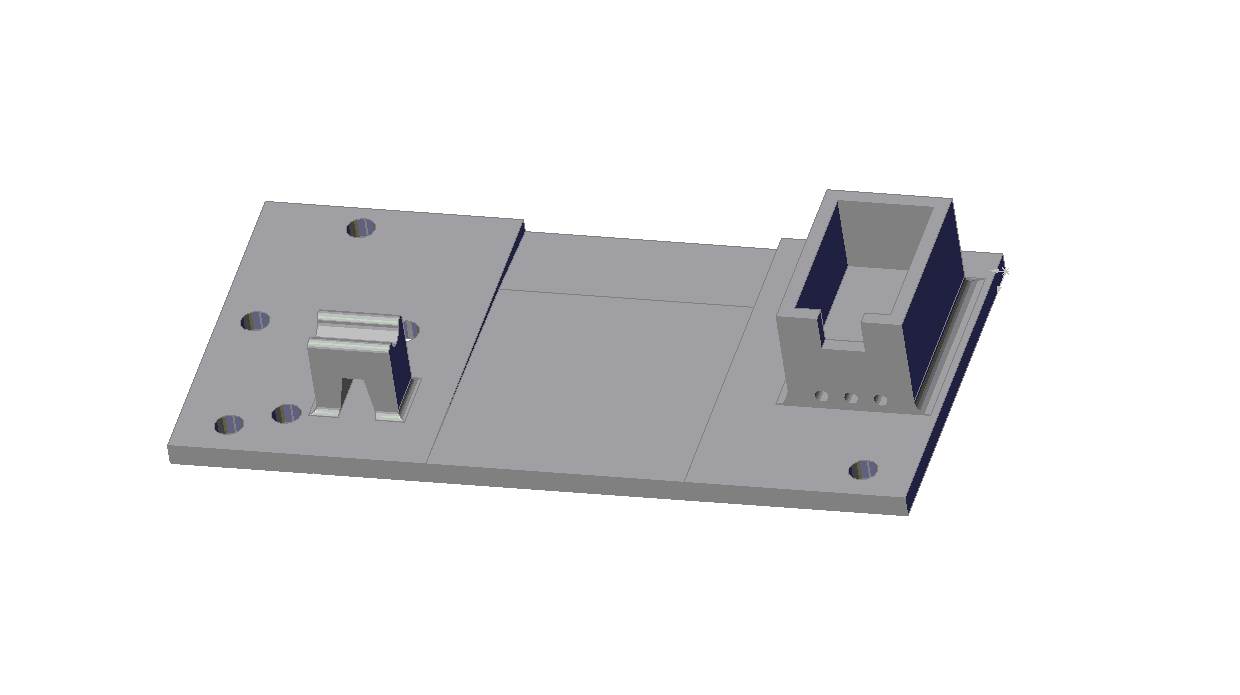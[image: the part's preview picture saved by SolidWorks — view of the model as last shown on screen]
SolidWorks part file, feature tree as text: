
SOLIDWORKS PART (.sldprt)
format: sldprt  version: not decoded by parser v0  size: 579,072 bytes
history: native  units: mm
features: sketch x13, cut_extrude x8, fillet x8, extrude x5, plane x3, material x1 (+10 scaffold rows collapsed)
feature tree (48):
  scaffold x10  (default folders/planes/origin — collapsed)
  material  "Matériau <non spécifié>"
  plane  "Plan de face"
  plane  "Plan de dessus"
  plane  "Plan de droite"
  sketch  "Esquisse1"  dims[D1=100.0mm D2=50.0mm]
  extrude  "Extrusion1"  Depth=1mm
  sketch  "Esquisse2"  dims[D1=30.0mm D2=35.0mm D3=35.0mm]
  extrude  "Extrusion2"  Depth=2mm
  sketch  "Esquisse4"  dims[D1=17.0mm D2=26.0mm]
  extrude  "Extrusion3"  Depth=15mm
  sketch  "Esquisse5"  dims[D1=2.0mm D2=2.0mm]
  cut_extrude  "Enlèv. mat.-Extru.1"  Depth=11mm
  sketch  "Esquisse6"  dims[D1=15.0mm D2=3.5mm]
  cut_extrude  "Enlèv. mat.-Extru.2"  Depth=4mm
  sketch  "Esquisse7"  dims[D1=6.0mm D2=3.5mm]
  cut_extrude  "Enlèv. mat.-Extru.3"  Depth=5mm
  sketch  "Esquisse8"  dims[D1=6.5mm D2=4.0mm D3=4.0mm]
  cut_extrude  "Enlèv. mat.-Extru.4"  Depth=8mm
  sketch  "Esquisse10"  dims[D1=7.0mm D2=5.0mm D3=5.0mm D4=7.0mm D5=38.0mm D6=14.0mm D7=14.0mm]
  cut_extrude  "Enlèv. mat.-Extru.5"  [1 undecoded]
  fillet  "Congé1"  Radius=2mm
  fillet  "Congé2"  Radius=2mm
  fillet  "Congé3"  Radius=2mm
  sketch  "Esquisse12"
  extrude  "Extrusion5"  Depth=18mm
  sketch  "Esquisse13"  dims[D1=2.0mm]
  cut_extrude  "Enlèv. mat.-Extru.8"  Depth=15mm
  fillet  "Congé6"  Radius=1mm
  fillet  "Congé7"  Radius=1mm
  sketch  "Esquisse14"  dims[D1=3.0mm D2=3.0mm D3=6.0mm]
  cut_extrude  "Enlèv. mat.-Extru.9"  [1 undecoded]
  sketch  "Esquisse15"  dims[D1=20.0mm]
  cut_extrude  "Enlèv. mat.-Extru.10"  [1 undecoded]
  fillet  "Congé8"  Radius=1mm
  fillet  "Congé9"  Radius=1mm
  fillet  "Congé10"  Radius=1mm
  sketch  "Esquisse16"
  extrude  "Extrusion6"  Depth=35mm
decode coverage: 29 of 34 modeling features carry decoded parameters
note: 3 parameter values undecoded
summary: no parameter record found for 3 features
note: suppression state not decoded; provenance and decode notes live in map.json
